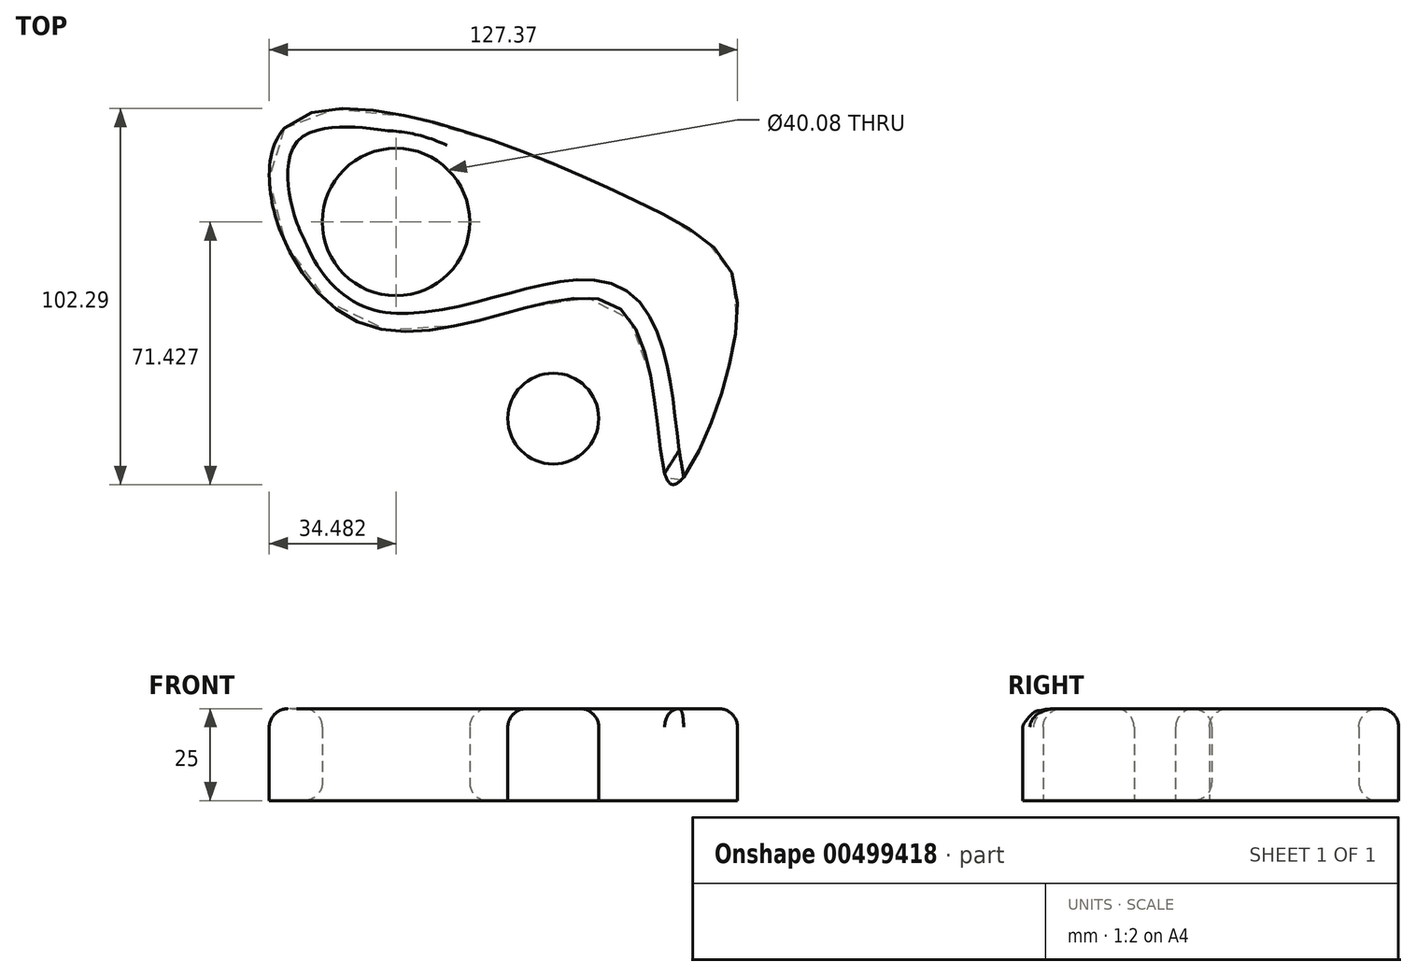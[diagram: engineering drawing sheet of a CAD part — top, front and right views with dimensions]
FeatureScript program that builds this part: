
annotation { "Feature Type Name" : "Feature", "Feature Type Description" : "" }
export const myFeature = defineFeature(function(context is Context, id is Id, definition is map)
    precondition{}
    {
        {
            var Q0;
            Q0=qCreatedBy(makeId("Top.planeOp"),FACE);
            var sketch = newSketch(context, id + "F0", { "sketchPlane" : qUnion([Q0])});
            skFitSpline(sketch, "E0", {"points": [v(-65.04, 48.56) * mm, v(33.12, 27.52) * mm, v(58.14, 0) * mm, v(42.26, -47.7) * mm, v(38.64, -46.32) * mm, v(25.36, 0) * mm, v(-43.47, -4.92) * mm, v(-65.04, 48.56) * mm]});
            skCircle(sketch, "E1", {"center": v(-34.75, 23) * mm, "radius": 20.04 * mm});
            skPoint(sketch, "E1.first.point", {"position": v(-50.72, 35.1) * mm});
            skPoint(sketch, "E1.second.point", {"position": v(-16.56, 14.58) * mm});
            skPoint(sketch, "E1.third.point", {"position": v(-54.69, 20.96) * mm});
            skCircle(sketch, "E2", {"center": v(8.02, -30.48) * mm, "radius": 12.36 * mm});
            skPoint(sketch, "E2.first.point", {"position": v(-2.93, -24.75) * mm});
            skPoint(sketch, "E2.second.point", {"position": v(17.08, -38.9) * mm});
            skPoint(sketch, "E2.third.point", {"position": v(-4.31, -31.31) * mm});
            skSolve(sketch);
        }
        {
            var Q0;
            Q0=makeQuery(id+"F0.imprint","IMPRINT",FACE,{"disambiguationData":[TD([[makeQuery(id+"F0.imprint","IMPRINT",EDGE,{"derivedFrom":sQuery(id+"F0.wireOp",EDGE,"E0")}),-1.0]])]});
            var Q1;
            Q1=makeQuery(id+"F0.imprint","IMPRINT",FACE,{"disambiguationData":[TD([[makeQuery(id+"F0.imprint","IMPRINT",EDGE,{"derivedFrom":sQuery(id+"F0.wireOp",EDGE,"E2")}),1.0]])]});
            extrude(context, id + "F1", {"entities" : qUnion([Q0, Q1]), "endBound" : BoundingType.SYMMETRIC, "depth" : 25 * mm});
        }
        {
            var Q0;
            Q0=makeQuery(id+"F1.opExtrude","CAP_FACE",FACE,{"disambiguationData":[OSD([sQuery(id+"F0.wireOp",EDGE,"E0"),sQuery(id+"F0.wireOp",EDGE,"E1")])],"isStart":false});
            var Q1;
            Q1=makeQuery(id+"F1.opExtrude","CAP_FACE",FACE,{"disambiguationData":[OSD([sQuery(id+"F0.wireOp",EDGE,"E2")])],"isStart":false});
            var Q2;
            Q2=makeQuery(id+"F1.opExtrude","SWEPT_FACE",FACE,{"disambiguationData":[OSD([sQuery(id+"F0.wireOp",EDGE,"E1")])]});
            fillet(context, id + "F2", {"entities" : qUnion([Q0, Q1, Q2]), "radius" : 5 * mm, "tangentPropagation" : true, "allowEdgeOverflow" : false});
        }
    });
